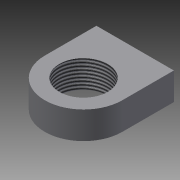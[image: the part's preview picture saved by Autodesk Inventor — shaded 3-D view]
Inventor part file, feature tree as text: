
AUTODESK INVENTOR PART (.ipt)
format: ipt  version: 2013 (Build 170138000, 138)  size: 84,480 bytes
history: native  units: in
note: dims shown in document units (in); Inventor stores cm internally (conversion verified against a paired STEP export)
features: extrude x1, thread x1, sketch x1
ambient origin geometry x8: Origin, YZ Plane, XZ Plane, XY Plane, X Axis, Y Axis, Z Axis, Center Point
bodies: Solid1 (feature_tree)
feature tree (3):
  extrude  "Extrusion1"  Depth=1.5in
  thread  "Thread1"  [1 undecoded]
  sketch  "Sketch1"  dims[d0=0.9375in d2=1.5in d3=0.53in d4=0.0in d5=1.0in d6=0.0in d16=1.0in]
note: 1 required parameter value undecoded (feature->parameter linkage not recoverable at this tier; creation-order binding heuristic only, values carry confidence <= 0.55)
